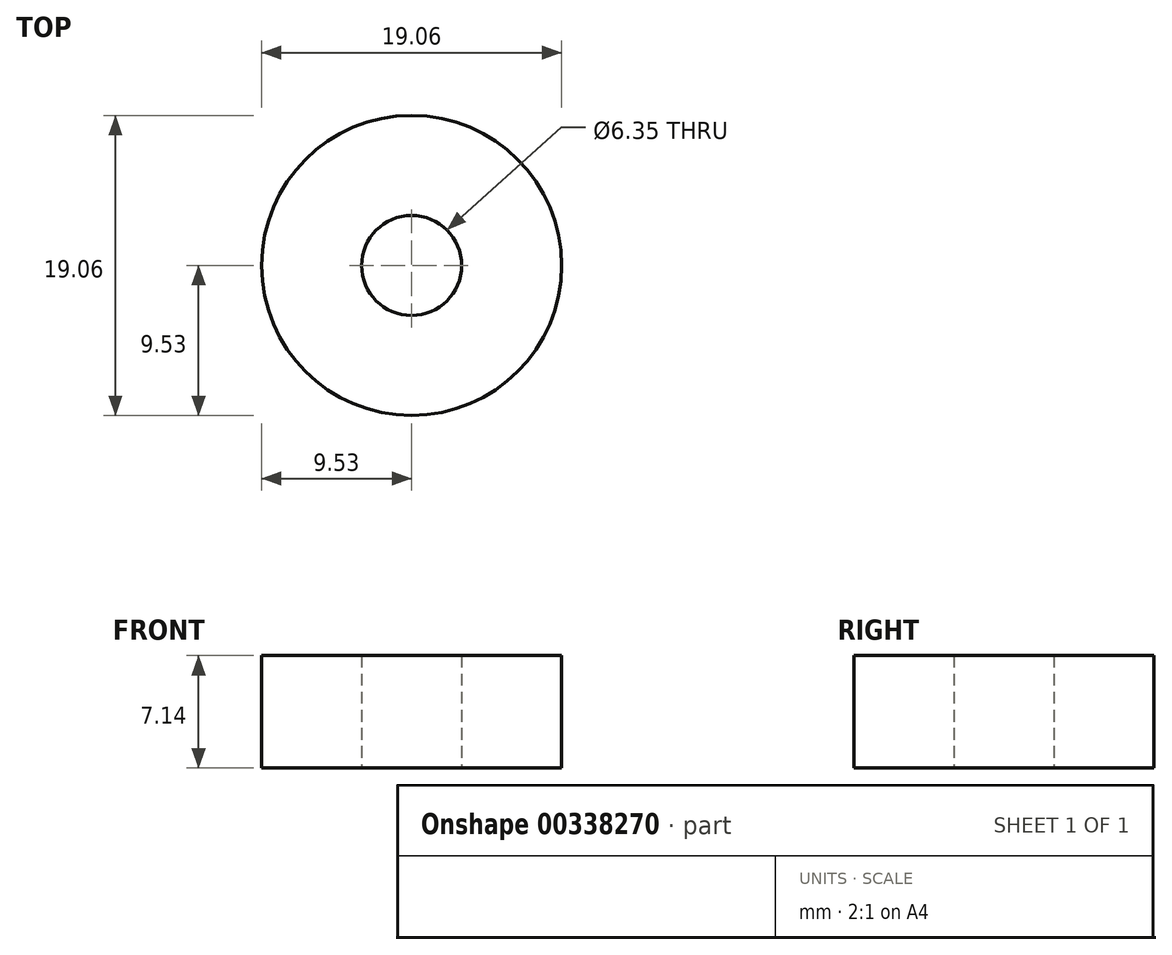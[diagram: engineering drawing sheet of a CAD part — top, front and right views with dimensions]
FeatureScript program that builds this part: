
annotation { "Feature Type Name" : "Feature", "Feature Type Description" : "" }
export const myFeature = defineFeature(function(context is Context, id is Id, definition is map)
    precondition{}
    {
        {
            var Q0;
            Q0=qCreatedBy(makeId("Top.planeOp"),FACE);
            var sketch = newSketch(context, id + "F0", { "sketchPlane" : qUnion([Q0])});
            skCircle(sketch, "E0", {"center": v(0, 0) * mm, "radius": 3.18 * mm});
            skCircle(sketch, "E1", {"center": v(0, 0) * mm, "radius": 9.53 * mm});
            skSolve(sketch);
        }
        {
            var Q0;
            Q0 = qSketchRegion(id + "F0", true);
            extrude(context, id + "F1", {"entities" : qUnion([Q0]), "depth" : 7.14 * mm});
        }
    });
